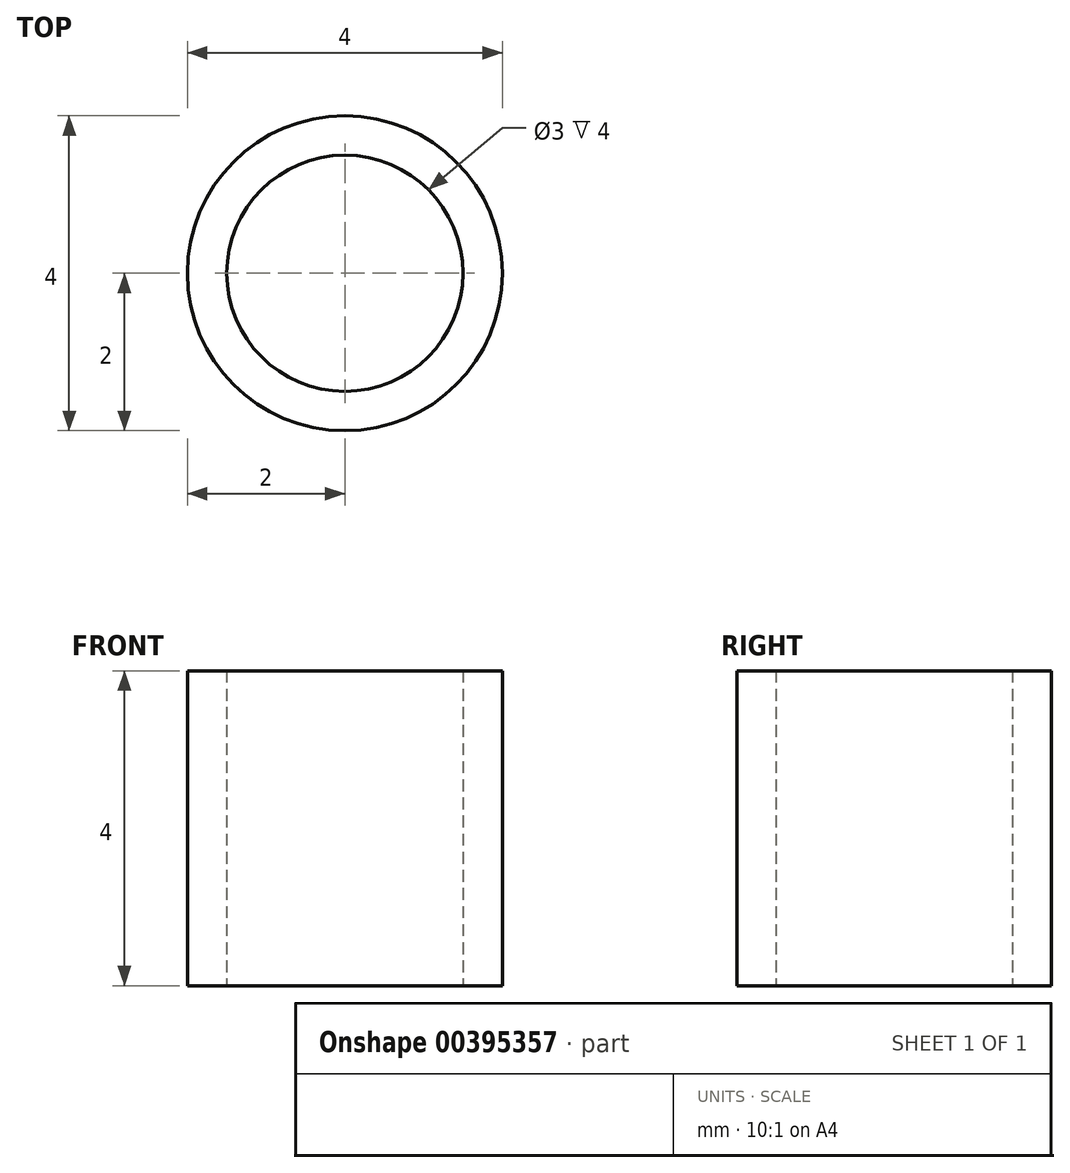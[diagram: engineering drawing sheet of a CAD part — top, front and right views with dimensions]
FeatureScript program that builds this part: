
annotation { "Feature Type Name" : "Feature", "Feature Type Description" : "" }
export const myFeature = defineFeature(function(context is Context, id is Id, definition is map)
    precondition{}
    {
        {
            var Q0;
            Q0=qCreatedBy(makeId("Top.planeOp"),FACE);
            var sketch = newSketch(context, id + "F0", { "sketchPlane" : qUnion([Q0])});
            skCircle(sketch, "E0", {"center": v(0, 0) * mm, "radius": 1.5 * mm});
            skCircle(sketch, "E1", {"center": v(0, 0) * mm, "radius": 2 * mm});
            skSolve(sketch);
        }
        {
            var Q0;
            Q0=makeQuery(id+"F0.imprint","IMPRINT",FACE,{"disambiguationData":[TD([[makeQuery(id+"F0.imprint","IMPRINT",EDGE,{"derivedFrom":sQuery(id+"F0.wireOp",EDGE,"E0")}),-1.0]])]});
            extrude(context, id + "F1", {"entities" : qUnion([Q0]), "depth" : 4 * mm});
        }
    });
